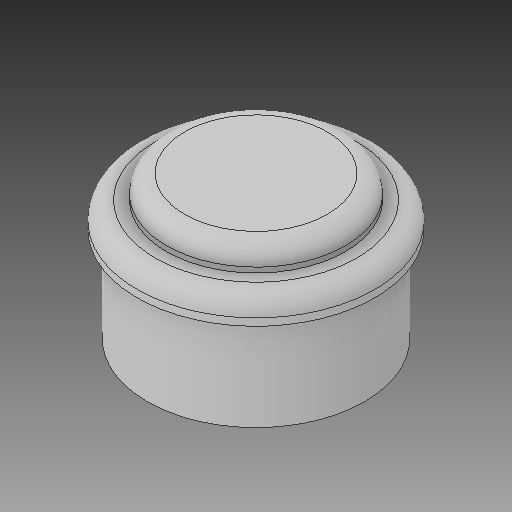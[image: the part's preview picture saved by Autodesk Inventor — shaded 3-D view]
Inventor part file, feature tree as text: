
AUTODESK INVENTOR PART (.ipt)
format: ipt  version: 2017 (Build 210142000, 142)  size: 162,816 bytes
history: native  units: in
note: dims shown in document units (in); Inventor stores cm internally (conversion verified against a paired STEP export)
features: extrude x3, sketch x3, fillet x2
ambient origin geometry x8: Origin, YZ Plane, XZ Plane, XY Plane, X Axis, Y Axis, Z Axis, Center Point
bodies: Solid1 (feature_tree)
feature tree (8):
  extrude  "Extrusion1"  Depth=0.1378in TaperAngle=0.0deg
  extrude  "Extrusion2"  Depth=0.126in TaperAngle=0.0deg
  fillet  "Fillet1"  Radius=0.0984in
  fillet  "Fillet2"  Radius=0.0984in
  extrude  "Extrusion3"  Depth=0.5157in TaperAngle=0.0deg
  sketch  "Sketch1"  dims[d0=1.2913in d1=0.1378in d2=0.0in]
  sketch  "Sketch2"  dims[d3=0.9724in d4=0.126in d5=0.0in d6=0.0984in d7=0.0984in]
  sketch  "Sketch3"  dims[d8=1.1811in d9=0.5157in d10=0.0in]
